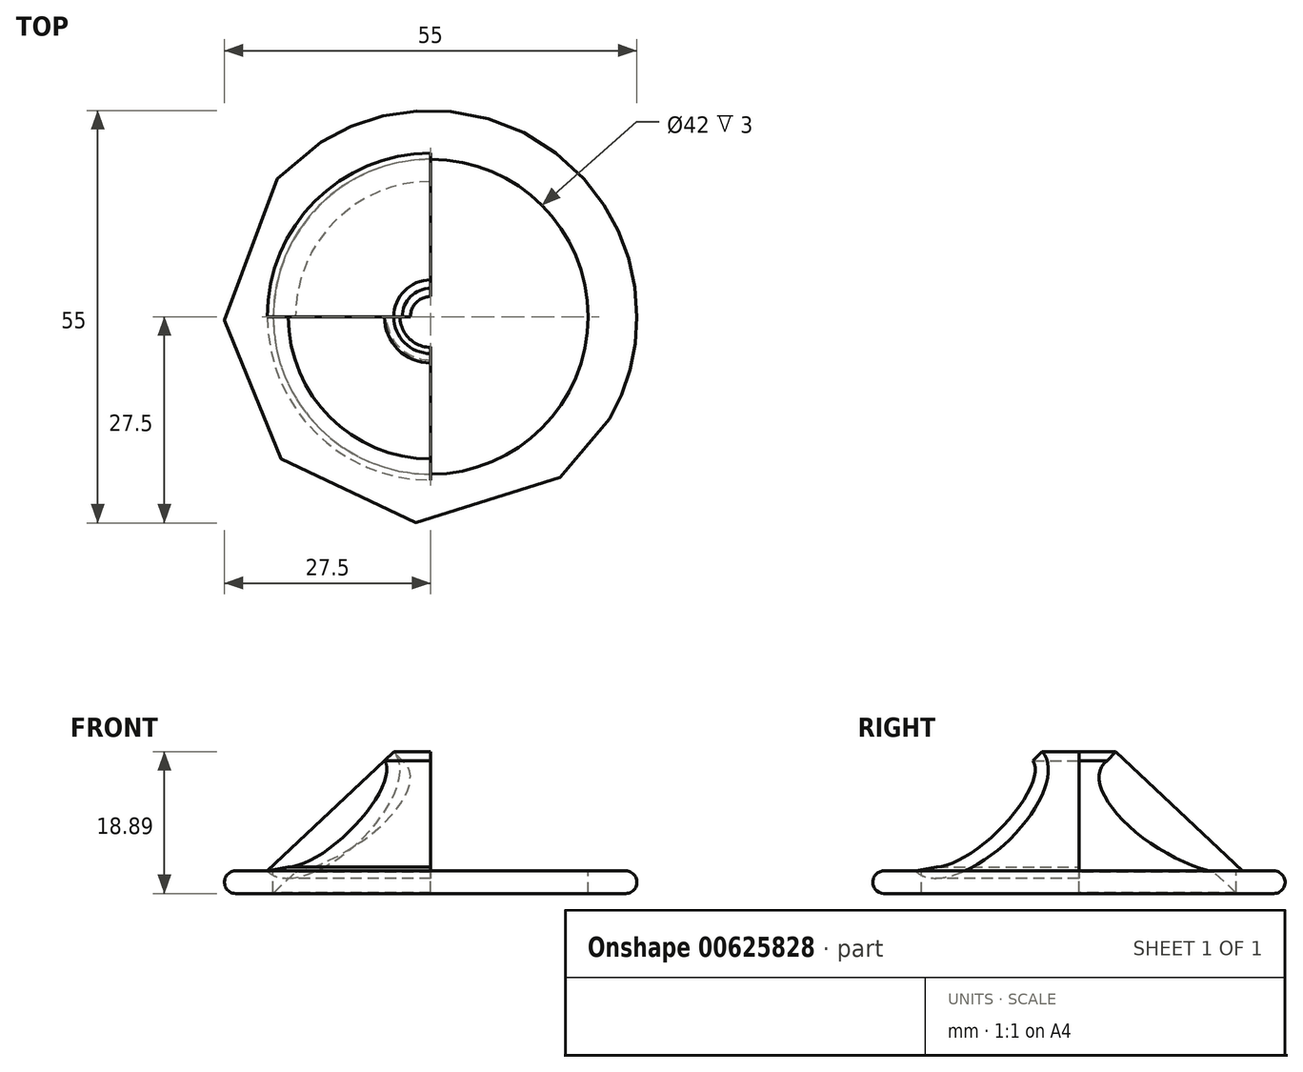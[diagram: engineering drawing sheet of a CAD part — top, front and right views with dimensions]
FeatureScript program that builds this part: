
annotation { "Feature Type Name" : "Feature", "Feature Type Description" : "" }
export const myFeature = defineFeature(function(context is Context, id is Id, definition is map)
    precondition{}
    {
        {
            var Q0;
            Q0=qCreatedBy(makeId("Front.planeOp"),FACE);
            var sketch = newSketch(context, id + "F0", { "sketchPlane" : qUnion([Q0])});
            skArc(sketch, "E0", {"start": v(-26, 16.5) * mm, "mid": v(-27.5, 15) * mm, "end": v(-26, 13.5) * mm});
            skLineSegment(sketch, "E1", {"start": v(0, 41) * mm, "end": v(0, -15.82) * mm, "construction": true});
            skLineSegment(sketch, "E2", {"start": v(-26, 15) * mm, "end": v(-26, 20.83) * mm, "construction": true});
            skLineSegment(sketch, "E3", {"start": v(-26, 15) * mm, "end": v(-26, 11.16) * mm, "construction": true});
            skPoint(sketch, "E4", {"position": v(-26, 16.5) * mm});
            skPoint(sketch, "E5", {"position": v(-26, 13.5) * mm});
            skLineSegment(sketch, "E6", {"start": v(-26, 16.5) * mm, "end": v(-21, 16.5) * mm});
            skLineSegment(sketch, "E7", {"start": v(-21, 16.5) * mm, "end": v(-21, 13.5) * mm});
            skLineSegment(sketch, "E8", {"start": v(-26, 13.5) * mm, "end": v(-21, 13.5) * mm});
            skSolve(sketch);
        }
        {
            var Q0;
            Q0 = qSketchRegion(id + "F0", true);
            var Q1;
            Q1=sQuery(id+"F0.wireOp",EDGE,"E1");
            revolve(context, id + "F1", {"entities" : qUnion([Q0]), "axis" : qUnion([Q1]), "revolveType" : RevolveType.FULL});
        }
        {
            var Q0;
            Q0=qCreatedBy(makeId("Front.planeOp"),FACE);
            var sketch = newSketch(context, id + "F2", { "sketchPlane" : qUnion([Q0])});
            skLineSegment(sketch, "E9", {"start": v(-20.97, 13.56) * mm, "end": v(-18.03, 16.33) * mm});
            skLineSegment(sketch, "E10", {"start": v(-3.05, 30.4) * mm, "end": v(-4.9, 32.37) * mm});
            skLineSegment(sketch, "E11", {"start": v(-4.9, 32.37) * mm, "end": v(-22.82, 15.53) * mm});
            skLineSegment(sketch, "E12", {"start": v(-20.97, 13.56) * mm, "end": v(-22.82, 15.53) * mm});
            skLineSegment(sketch, "E13", {"start": v(0, 39.1) * mm, "end": v(0, 9.24) * mm, "construction": true});
            skEllipticalArc(sketch, "E14", {});
            skLineSegment(sketch, "E15", {"start": v(0, 44.27) * mm, "end": v(0, 0) * mm, "construction": true});
            const initialGuessF2  = {"E14": [-0.013863650817886822, 0.023951457211260206, 0.8588499684494668, 0.5122272266234489, 0.012589696740095004, 0.005491515218516992, 4.076042466231861, 0.1913811194120911]};
            skSetInitialGuess(sketch, initialGuessF2);
            skSolve(sketch);
        }
        {
            var Q0;
            Q0 = qSketchRegion(id + "F2", true);
            var Q1;
            Q1=sQuery(id+"F2.wireOp",EDGE,"E13");
            revolve(context, id + "F3", {"operationType" : NewBodyOperationType.ADD, "entities" : qUnion([Q0]), "axis" : qUnion([Q1]), "revolveType" : RevolveType.ONE_DIRECTION, "angle" : 90 * degree});
        }
        {
            var Q0;
            Q0=qCreatedBy(makeId("Front.planeOp"),FACE);
            var sketch = newSketch(context, id + "F4", { "sketchPlane" : qUnion([Q0])});
            skLineSegment(sketch, "E16", {"start": v(-20.55, 17.67) * mm, "end": v(-20.55, 17.67) * mm});
            skLineSegment(sketch, "E17.trimOffspring", {"start": v(-6.16, 31.2) * mm, "end": v(-4.91, 32.39) * mm});
            skLineSegment(sketch, "E18", {"start": v(0, 39.22) * mm, "end": v(0, 11.17) * mm, "construction": true});
            skEllipticalArc(sketch, "E19.MirrorCS", {});
            skLineSegment(sketch, "E20", {"start": v(-21.78, 16.5) * mm, "end": v(-18.97, 17.04) * mm});
            skEllipticalArc(sketch, "E21.trimOffspring", {});
            skPoint(sketch, "E22.start.orphan", {"position": v(-21.8, 16.5) * mm});
            skLineSegment(sketch, "E23", {"start": v(-21.78, 16.5) * mm, "end": v(-21.78, 16.47) * mm});
            skPoint(sketch, "E24.orphan", {"position": v(-21.8, 16.49) * mm});
            skLineSegment(sketch, "E25", {"start": v(-6.16, 31.2) * mm, "end": v(-6.14, 31.19) * mm});
            skLineSegment(sketch, "E26", {"start": v(-4.91, 32.39) * mm, "end": v(-4.89, 32.36) * mm});
            const initialGuessF4  = {"E19.MirrorCS": [-0.01334645683241245, 0.02442767421042535, 0.7148928792873072, 0.6992339888365724, 0.009890762188483145, 0.0036477453269778185, 3.5205813128050245, 6.227502738553761], "E21.trimOffspring": [-0.0133464568324052, 0.024427674210417666, -0.7292488883380907, -0.6842485358827297, 0.011596491900515607, 0.005535628728408914, 0.005294042132371371, 3.141592653589793]};
            skSetInitialGuess(sketch, initialGuessF4);
            skSolve(sketch);
        }
        {
            var Q0;
            Q0 = qSketchRegion(id + "F4", true);
            var Q1;
            Q1=sQuery(id+"F4.wireOp",EDGE,"E18");
            revolve(context, id + "F5", {"entities" : qUnion([Q0]), "axis" : qUnion([Q1]), "revolveType" : RevolveType.ONE_DIRECTION, "oppositeDirection" : true, "angle" : 90 * degree});
        }
    });
